FCSTD DOCUMENT  (FreeCAD 0.21R33668 +26 (Git))
Label: bushing sketch
License: All rights reserved
LicenseURL: https://en.wikipedia.org/wiki/All_rights_reserved
objects: Sketcher::SketchObject×3, PartDesign::Body×1
note: 4 computed .brp shape members not serialized (recipe doc carries the construction recipe); baked Part::Feature solids carry a one-line shape summary decoded from their .brp

FEATURE [Sketcher::SketchObject] Sketch
  FullyConstrained = false
  MapMode = 5
  Placement = pos=(0,0,0) rot=(1,0,0;1.5708rad)
  Support = -> [XZ_Plane]
  sketch-geometry (66):
    g0: LineSegment StartX=-3.3 StartY=0 StartZ=0 EndX=3.3 EndY=0 EndZ=0
    g1: LineSegment StartX=-3.3 StartY=0 StartZ=0 EndX=-3.3 EndY=-2 EndZ=0
    g2: LineSegment StartX=-3.3 StartY=-2 StartZ=0 EndX=-3.4 EndY=-2 EndZ=0
    g3: LineSegment StartX=-3.4 StartY=-2 StartZ=0 EndX=-3.4 EndY=-4.50007 EndZ=0
    g4: LineSegment StartX=-3.4 StartY=-4.50007 StartZ=0 EndX=-6.25 EndY=-4.50007 EndZ=0
    g5: LineSegment StartX=3.3 StartY=0 StartZ=0 EndX=3.3 EndY=-2 EndZ=0
    g6: LineSegment StartX=3.3 StartY=-2 StartZ=0 EndX=3.4 EndY=-2 EndZ=0
    g7: LineSegment StartX=3.4 StartY=-2 StartZ=0 EndX=3.4 EndY=-4.50007 EndZ=0
    g8: LineSegment StartX=3.4 StartY=-4.50007 StartZ=0 EndX=6.25 EndY=-4.50007 EndZ=0
    g9: LineSegment StartX=-3 StartY=0 StartZ=0 EndX=-3 EndY=1.5 EndZ=0
    g10: LineSegment StartX=-3 StartY=1.5 StartZ=0 EndX=-1.5 EndY=1.5 EndZ=0
    g11: LineSegment StartX=-1.5 StartY=1.5 StartZ=0 EndX=-1.5 EndY=8.5 EndZ=0
    g12: LineSegment StartX=-1.5 StartY=8.5 StartZ=0 EndX=3 EndY=8.5 EndZ=0
    g13: LineSegment StartX=3 StartY=8.5 StartZ=0 EndX=3 EndY=0 EndZ=0
    g14: LineSegment StartX=-3.15 StartY=0.999931 StartZ=0 EndX=-2.95 EndY=0.499931 EndZ=0
    g15: LineSegment StartX=-2.95 StartY=0.499931 StartZ=0 EndX=-3.15 EndY=-6.9e-05 EndZ=0
    g16: LineSegment StartX=-3.6 StartY=-6.9e-05 StartZ=0 EndX=-3.6 EndY=-1.00007 EndZ=0
    g17: LineSegment StartX=-3.6 StartY=-1.00007 StartZ=0 EndX=-3.3 EndY=-1.50007 EndZ=0
    g18: LineSegment StartX=-3.3 StartY=-1.50007 StartZ=0 EndX=-3.6 EndY=-2.00007 EndZ=0
    g19: LineSegment StartX=-3.6 StartY=-2.00007 StartZ=0 EndX=-3.6 EndY=-3.50007 EndZ=0
    g20: LineSegment StartX=-3.6 StartY=-3.50007 StartZ=0 EndX=-3.35 EndY=-4.00007 EndZ=0
    g21: LineSegment StartX=-3.35 StartY=-4.00007 StartZ=0 EndX=-3.85 EndY=-4.50007 EndZ=0
    g22: LineSegment StartX=-3.85 StartY=-4.50007 StartZ=0 EndX=-4.4 EndY=-4.50007 EndZ=0
    g23: LineSegment StartX=-4.4 StartY=-4.50007 StartZ=0 EndX=-4.4 EndY=-4.05007 EndZ=0
    g24: LineSegment StartX=-4.4 StartY=-4.05007 StartZ=0 EndX=-5.75 EndY=-4.05007 EndZ=0
    g25: LineSegment StartX=-5.75 StartY=-4.05007 StartZ=0 EndX=-5.75 EndY=-3.60007 EndZ=0
    g26: LineSegment StartX=-5.75 StartY=-3.60007 StartZ=0 EndX=-4.675 EndY=-3.60007 EndZ=0
    g27: LineSegment StartX=-4.675 StartY=-3.60007 StartZ=0 EndX=-4.675 EndY=-2.30007 EndZ=0
    g28: LineSegment StartX=-4.4 StartY=-2.02507 StartZ=0 EndX=-4.4 EndY=0.249931 EndZ=0
    g29: LineSegment StartX=-4.4 StartY=0.249931 StartZ=0 EndX=-3.65 EndY=0.999931 EndZ=0
    g30: LineSegment StartX=-3.65 StartY=0.999931 StartZ=0 EndX=-3.15 EndY=0.999931 EndZ=0
    g31: LineSegment StartX=-3.6 StartY=-6.9e-05 StartZ=0 EndX=-3.15 EndY=-6.9e-05 EndZ=0
    g32: LineSegment StartX=3.15 StartY=0.999931 StartZ=0 EndX=2.95 EndY=0.499931 EndZ=0
    g33: LineSegment StartX=2.95 StartY=0.499931 StartZ=0 EndX=3.15 EndY=-6.9e-05 EndZ=0
    g34: LineSegment StartX=3.5 StartY=-6.9e-05 StartZ=0 EndX=3.5 EndY=-1.00007 EndZ=0
    g35: LineSegment StartX=3.5 StartY=-1.00007 StartZ=0 EndX=3.3 EndY=-1.50007 EndZ=0
    g36: LineSegment StartX=3.3 StartY=-1.50007 StartZ=0 EndX=3.5 EndY=-2.00007 EndZ=0
    g37: LineSegment StartX=3.5 StartY=-2.00007 StartZ=0 EndX=3.5 EndY=-3.50007 EndZ=0
    g38: LineSegment StartX=3.5 StartY=-3.50007 StartZ=0 EndX=3.35 EndY=-4.00007 EndZ=0
    g39: LineSegment StartX=3.35 StartY=-4.00007 StartZ=0 EndX=3.85 EndY=-4.50007 EndZ=0
    g40: LineSegment StartX=3.85 StartY=-4.50007 StartZ=0 EndX=4.4 EndY=-4.50007 EndZ=0
    g41: LineSegment StartX=4.4 StartY=-4.50007 StartZ=0 EndX=4.4 EndY=-4.05007 EndZ=0
    g42: LineSegment StartX=4.4 StartY=-4.05007 StartZ=0 EndX=5.75 EndY=-4.05007 EndZ=0
    g43: LineSegment StartX=5.75 StartY=-4.05007 StartZ=0 EndX=5.75 EndY=-3.60007 EndZ=0
    g44: LineSegment StartX=5.75 StartY=-3.60007 StartZ=0 EndX=4.675 EndY=-3.60007 EndZ=0
    g45: LineSegment StartX=4.675 StartY=-3.60007 StartZ=0 EndX=4.675 EndY=-2.30007 EndZ=0
    g46: LineSegment StartX=4.4 StartY=-2.02507 StartZ=0 EndX=4.4 EndY=0.249931 EndZ=0
    g47: LineSegment StartX=4.4 StartY=0.249931 StartZ=0 EndX=3.65 EndY=0.999931 EndZ=0
    g48: LineSegment StartX=3.65 StartY=0.999931 StartZ=0 EndX=3.15 EndY=0.999931 EndZ=0
    g49: LineSegment StartX=3.5 StartY=-6.9e-05 StartZ=0 EndX=3.15 EndY=-6.9e-05 EndZ=0
    g50: LineSegment StartX=-6.25 StartY=-4.50007 StartZ=0 EndX=-6.25 EndY=-10.8 EndZ=0
    g51: LineSegment StartX=-6.25 StartY=-10.8 StartZ=0 EndX=6.25 EndY=-10.8 EndZ=0
    g52: LineSegment StartX=6.25 StartY=-10.8 StartZ=0 EndX=6.25 EndY=-4.50007 EndZ=0
    g53: LineSegment StartX=-13.8517 StartY=-10.8 StartZ=0 EndX=17.8649 EndY=-10.8 EndZ=0
    g54: LineSegment StartX=-12.656 StartY=-1.14 StartZ=0 EndX=12.2568 EndY=-1.14 EndZ=0
    g55: LineSegment StartX=12.2568 StartY=-1.14 StartZ=0 EndX=12.2568 EndY=-2.14 EndZ=0
    g56: LineSegment StartX=12.2568 StartY=-2.14 StartZ=0 EndX=-12.656 EndY=-2.14 EndZ=0
    g57: LineSegment StartX=-12.656 StartY=-2.14 StartZ=0 EndX=-12.656 EndY=-1.14 EndZ=0
    g58: LineSegment StartX=-4.675 StartY=-2.30007 StartZ=0 EndX=-4.4 EndY=-2.02507 EndZ=0
    g59: LineSegment StartX=4.675 StartY=-2.30007 StartZ=0 EndX=4.4 EndY=-2.02507 EndZ=0
    g60: LineSegment StartX=-13.8517 StartY=-10.8 StartZ=0 EndX=-13.8517 EndY=-12.24 EndZ=0
    g61: LineSegment StartX=-13.8517 StartY=-12.24 StartZ=0 EndX=17.8649 EndY=-12.24 EndZ=0
    g62: LineSegment StartX=17.8649 StartY=-12.24 StartZ=0 EndX=17.8649 EndY=-10.8 EndZ=0
    g63: LineSegment StartX=-2.44854 StartY=-12.24 StartZ=0 EndX=-2.44854 EndY=-16.14 EndZ=0
    g64: LineSegment StartX=-2.44854 StartY=-16.14 StartZ=0 EndX=4.63678 EndY=-16.14 EndZ=0
    g65: LineSegment StartX=4.63678 StartY=-16.14 StartZ=0 EndX=4.63678 EndY=-12.24 EndZ=0
  constraints (196):
    c: PointOnObject(g0,g-1)
    c: Symmetric(g0,g0,g-1)
    c: Coincident(g1,g0)
    c: Vertical(g1)
    c: Horizontal(g2)
    c: Coincident(g3,g2)
    c: Vertical(g3)
    c: Coincident(g4,g3)
    c: Horizontal(g4)
    c: Coincident(g2,g1)
    c: Coincident(g5,g0)
    c: Vertical(g5)
    c: Coincident(g6,g5)
    c: Horizontal(g6)
    c: Coincident(g7,g6)
    c: Vertical(g7)
    c: Coincident(g8,g7)
    c: Horizontal(g8)
    c: Equal(g6,g2)
    c: Equal(g3,g7)
    c: Equal(g8,g4)
    c: Equal(g5,g1)
    c: PointOnObject(g9,g0)
    c: Coincident(g10,g9)
    c: Vertical(g11)
    c: Horizontal(g12)
    c: Vertical(g13)
    c: Coincident(g13,g12)
    c: Coincident(g12,g11)
    c: Horizontal(g10)
    c: Vertical(g9)
    c: Coincident(g11,g10)
    c: DistanceY(g1,g1) = 2
    c: DistanceX(g0,g0) = 6.6
    c: DistanceX(g3,g7) = 6.8
    c: Symmetric(g9,g13,g-1)
    c: DistanceX(g9,g13) = 6
    c: DistanceX(g12,g12) = 4.5
    c: Coincident(g15,g14)
    c: Vertical(g16)
    c: Coincident(g18,g17)
    c: Coincident(g19,g18)
    c: Vertical(g19)
    c: Coincident(g20,g19)
    c: Coincident(g21,g20)
    c: Horizontal(g22)
    c: Coincident(g24,g23)
    c: Horizontal(g24)
    c: Coincident(g25,g24)
    c: Vertical(g25)
    c: Coincident(g26,g25)
    c: Horizontal(g26)
    c: Coincident(g27,g26)
    c: Vertical(g27)
    c: Vertical(g28)
    c: Coincident(g29,g28)
    c: Coincident(g30,g14)
    c: Coincident(g30,g29)
    c: Coincident(g21,g22)
    c: Horizontal(g30)
    c: DistanceX(g28,g29) = 0.75
    c: Angle(g29,g30) = 2.35619
    c: DistanceX(g30,g30) = 0.5
    c: DistanceX(g14,g-1) = 2.95
    c: DistanceY(g15,g14) = 1
    c: Equal(g14,g15)
    c: Coincident(g16,g17)
    c: Vertical(g16,g18)
    c: Equal(g17,g18)
    c: DistanceX(g17,g-1) = 3.3
    c: DistanceX(g20,g-1) = 3.35
    c: Coincident(g22,g23)
    c: Vertical(g23)
    c: Angle(g21,g22) = 2.35619
    c: DistanceY(g27,g27) = 1.3
    c: DistanceY(g23,g23) = 0.45
    c: DistanceX(g24,g-1) = 5.75
    c: DistanceX(g22,g-1) = 4.4
    c: DistanceY(g21,g19) = 1
    c: DistanceY(g18,g16) = 1
    c: DistanceX(g26,g-1) = 4.675
    c: DistanceY(g22,g15) = 4.5
    c: DistanceY(g21,g20) = 0.5
    c: DistanceY(g21,g17) = 3
    c: Coincident(g31,g16)
    c: Coincident(g31,g15)
    c: Horizontal(g31)
    c: DistanceX(g16,g-1) = 3.6
    c: Vertical(g14,g15)
    c: Coincident(g33,g32)
    c: Vertical(g34)
    c: Coincident(g36,g35)
    c: Coincident(g37,g36)
    c: Vertical(g37)
    c: Coincident(g38,g37)
    c: Coincident(g39,g38)
    c: Horizontal(g40)
    c: Coincident(g42,g41)
    c: Horizontal(g42)
    c: Coincident(g43,g42)
    c: Vertical(g43)
    c: Coincident(g44,g43)
    c: Horizontal(g44)
    c: Coincident(g45,g44)
    c: Vertical(g45)
    c: Vertical(g46)
    c: Coincident(g47,g46)
    c: Coincident(g48,g32)
    c: Coincident(g48,g47)
    c: Coincident(g39,g40)
    c: Horizontal(g48)
    c: Angle(g47,g48) = -2.35619
    c: Equal(g32,g33)
    c: Coincident(g34,g35)
    c: Equal(g35,g36)
    c: Coincident(g40,g41)
    c: Vertical(g41)
    c: Angle(g39,g40) = -2.35619
    c: Coincident(g49,g34)
    c: Coincident(g49,g33)
    c: Horizontal(g49)
    c: Equal(g16,g34)
    c: Equal(g19,g37)
    c: Equal(g22,g40)
    c: Equal(g14,g32)
    c: Equal(g30,g48)
    c: Equal(g29,g47)
    c: Equal(g45,g27)
    c: Equal(g26,g44)
    c: Equal(g25,g43)
    c: Equal(g24,g42)
    c: Equal(g23,g41)
    c: Vertical(g36,g34)
    c: Horizontal(g32,g14)
    c: Horizontal(g33,g15)
    c: Horizontal(g35,g17)
    c: Horizontal(g20,g38)
    c: DistanceX(g-1,g34) = 3.5
    c: DistanceX(g-1,g32) = 2.95
    c: DistanceX(g-1,g35) = 3.3
    c: DistanceX(g-1,g38) = 3.35
    c: DistanceY(g16,g16) = 1
    c: DistanceY(g22,g29) = 5.5
    c: DistanceX(g4,g8) = 12.5
    c: Coincident(g50,g4)
    c: Vertical(g50)
    c: Coincident(g51,g50)
    c: Horizontal(g51)
    c: Coincident(g52,g51)
    c: Coincident(g52,g8)
    c: Vertical(g52)
    c: Horizontal(g53)
    c: PointOnObject(g51,g53)
    c: Coincident(g54,g55)
    c: Coincident(g55,g56)
    c: Coincident(g56,g57)
    c: Coincident(g57,g54)
    c: Horizontal(g54)
    c: Horizontal(g56)
    c: Vertical(g55)
    c: Vertical(g57)
    c: DistanceY(g57,g57) = 1
    c: DistanceY(g4,g56) = 2.36007
    c: DistanceY(g26,g56) = 1.46007
    c: DistanceY(g22,g25) = 0.9
    c: Coincident(g58,g27)
    c: Coincident(g28,g58)
    c: Angle(g58) = 0.785398
    c: DistanceX(g28,g-1) = 4.4
    c: Coincident(g59,g45)
    c: Coincident(g46,g59)
    c: Angle(g59,g45) = 2.35619
    c: DistanceX(g-1,g46) = 4.4
    c: Horizontal(g39,g21)
    c: Coincident(g60,g53)
    c: Vertical(g60)
    c: Coincident(g61,g60)
    c: Horizontal(g61)
    c: Coincident(g62,g61)
    c: Coincident(g62,g53)
    c: Vertical(g62)
    c: PointOnObject(g63,g61)
    c: Vertical(g63)
    c: Coincident(g64,g63)
    c: Horizontal(g64)
    c: PointOnObject(g65,g61)
    c: Coincident(g65,g64)
    c: Vertical(g65)
    c: DistanceY(g60,g60) = 1.44
    c: DistanceY(g63,g63) = 3.9
    c: DistanceY(g65,g55) = 10.1
    c: DistanceY(g50,g0) = 10.8
    c: DistanceY(g25,g25) = 0.45
    c: DistanceY(g11,g11) = 7
    c: DistanceY(g9,g9) = 1.5
    c: PointOnObject(g21,g4)
FEATURE [Sketcher::SketchObject] Sketch001
  FullyConstrained = true
  MapMode = 5
  Support = -> [XY_Plane]
  sketch-geometry (9):
    g0: Circle CenterX=0 CenterY=0.075 CenterZ=0 NormalX=0 NormalY=0 NormalZ=1 AngleXU=0 Radius=4.875
    g1: Circle CenterX=0 CenterY=0.075 CenterZ=0 NormalX=0 NormalY=0 NormalZ=1 AngleXU=0 Radius=4.85
    g2: Circle CenterX=0 CenterY=0.075 CenterZ=0 NormalX=0 NormalY=0 NormalZ=1 AngleXU=0 Radius=4.825
    g3: Circle CenterX=0 CenterY=0 CenterZ=0 NormalX=0 NormalY=0 NormalZ=1 AngleXU=0 Radius=0.075
    g4: Circle CenterX=0 CenterY=0 CenterZ=0 NormalX=0 NormalY=0 NormalZ=1 AngleXU=0 Radius=4.95
    g5: Circle CenterX=0 CenterY=0 CenterZ=0 NormalX=0 NormalY=0 NormalZ=1 AngleXU=0 Radius=4.9
    g6: Circle CenterX=0 CenterY=0 CenterZ=0 NormalX=0 NormalY=0 NormalZ=1 AngleXU=0 Radius=4.675
    g7: LineSegment StartX=0 StartY=-4.675 StartZ=0 EndX=0 EndY=-4.75 EndZ=0
    g8: LineSegment StartX=0 StartY=4.675 StartZ=0 EndX=0 EndY=4.9 EndZ=0
  constraints (27):
    c: Coincident(g1,g0)
    c: Diameter(g0) = 9.75
    c: Diameter(g1) = 9.7
    c: Coincident(g2,g0)
    c: Diameter(g2) = 9.65
    c: Coincident(g3,g-1)
    c: Diameter(g3) = 0.15
    c: PointOnObject(g0,g3)
    c: Coincident(g4,g3)
    c: PointOnObject(g0,g-2)
    c: Tangent(g4,g0)
    c: Diameter(g4) = 9.9
    c: Coincident(g5,g3)
    c: Tangent(g5,g2)
    c: Diameter(g5) = 9.8
    c: Coincident(g6,g3)
    c: Diameter(g6) = 9.35
    c: PointOnObject(g7,g6)
    c: PointOnObject(g7,g2)
    c: Vertical(g7)
    c: PointOnObject(g7,g-2)
    c: DistanceY(g7,g7) = 0.075
    c: PointOnObject(g8,g6)
    c: PointOnObject(g8,g5)
    c: Vertical(g8)
    c: PointOnObject(g8,g-2)
    c: DistanceY(g8,g8) = 0.225
FEATURE [Sketcher::SketchObject] Sketch002
  FullyConstrained = false
  MapMode = 5
  Placement = pos=(0,0,0) rot=(1,0,0;1.5708rad)
  Support = -> [XZ_Plane]
  sketch-geometry (62):
    g0: LineSegment StartX=-3.35 StartY=0 StartZ=0 EndX=3.35 EndY=0 EndZ=0
    g1: LineSegment StartX=-3.35 StartY=0 StartZ=0 EndX=-3.35 EndY=-2 EndZ=0
    g2: LineSegment StartX=-3.35 StartY=-2 StartZ=0 EndX=-3.4 EndY=-2 EndZ=0
    g3: LineSegment StartX=-3.4 StartY=-2 StartZ=0 EndX=-3.4 EndY=-4.29691 EndZ=0
    g4: LineSegment StartX=-3.4 StartY=-4.29691 StartZ=0 EndX=-6.25 EndY=-4.29691 EndZ=0
    g5: LineSegment StartX=3.35 StartY=0 StartZ=0 EndX=3.35 EndY=-2 EndZ=0
    g6: LineSegment StartX=3.35 StartY=-2 StartZ=0 EndX=3.4 EndY=-2 EndZ=0
    g7: LineSegment StartX=3.4 StartY=-2 StartZ=0 EndX=3.4 EndY=-4.29691 EndZ=0
    g8: LineSegment StartX=3.4 StartY=-4.29691 StartZ=0 EndX=6.25 EndY=-4.29691 EndZ=0
    g9: LineSegment StartX=-3 StartY=0 StartZ=0 EndX=-3 EndY=1.5 EndZ=0
    g10: LineSegment StartX=-3 StartY=1.5 StartZ=0 EndX=-1.5 EndY=1.5 EndZ=0
    g11: LineSegment StartX=-1.5 StartY=1.5 StartZ=0 EndX=-1.5 EndY=8.5 EndZ=0
    g12: LineSegment StartX=-1.5 StartY=8.5 StartZ=0 EndX=3 EndY=8.5 EndZ=0
    g13: LineSegment StartX=3 StartY=8.5 StartZ=0 EndX=3 EndY=0 EndZ=0
    g14: LineSegment StartX=-3.15 StartY=1.20309 StartZ=0 EndX=-2.95 EndY=0.703087 EndZ=0
    g15: LineSegment StartX=-2.95 StartY=0.703087 StartZ=0 EndX=-3.15 EndY=0.203087 EndZ=0
    g16: LineSegment StartX=-3.3 StartY=-3.79691 StartZ=0 EndX=-3.8 EndY=-4.29691 EndZ=0
    g17: LineSegment StartX=-3.8 StartY=-4.29691 StartZ=0 EndX=-4.4 EndY=-4.29691 EndZ=0
    g18: LineSegment StartX=-4.4 StartY=-4.29691 StartZ=0 EndX=-4.4 EndY=-3.84691 EndZ=0
    g19: LineSegment StartX=-4.4 StartY=-3.84691 StartZ=0 EndX=-5.75 EndY=-3.84691 EndZ=0
    g20: LineSegment StartX=-5.75 StartY=-3.84691 StartZ=0 EndX=-5.75 EndY=-3.39691 EndZ=0
    g21: LineSegment StartX=-5.75 StartY=-3.39691 StartZ=0 EndX=-4.675 EndY=-3.39691 EndZ=0
    g22: LineSegment StartX=-4.675 StartY=-3.39691 StartZ=0 EndX=-4.675 EndY=-2.09691 EndZ=0
    g23: LineSegment StartX=-4.4 StartY=-1.82191 StartZ=0 EndX=-4.4 EndY=0.453087 EndZ=0
    g24: LineSegment StartX=-4.4 StartY=0.453087 StartZ=0 EndX=-3.65 EndY=1.20309 EndZ=0
    g25: LineSegment StartX=-3.65 StartY=1.20309 StartZ=0 EndX=-3.15 EndY=1.20309 EndZ=0
    g26: LineSegment StartX=-3.3 StartY=0.203087 StartZ=0 EndX=-3.15 EndY=0.203087 EndZ=0
    g27: LineSegment StartX=3.15 StartY=1.20309 StartZ=0 EndX=2.95 EndY=0.703087 EndZ=0
    g28: LineSegment StartX=2.95 StartY=0.703087 StartZ=0 EndX=3.15 EndY=0.203087 EndZ=0
    g29: LineSegment StartX=3.5 StartY=0.203087 StartZ=0 EndX=3.5 EndY=-1.00007 EndZ=0
    g30: LineSegment StartX=3.5 StartY=-1.00007 StartZ=0 EndX=3.3 EndY=-1.50007 EndZ=0
    g31: LineSegment StartX=3.3 StartY=-1.50007 StartZ=0 EndX=3.5 EndY=-2.00007 EndZ=0
    g32: LineSegment StartX=3.5 StartY=-2.00007 StartZ=0 EndX=3.5 EndY=-3.50007 EndZ=0
    g33: LineSegment StartX=3.5 StartY=-3.50007 StartZ=0 EndX=3.35 EndY=-3.79691 EndZ=0
    g34: LineSegment StartX=3.35 StartY=-3.79691 StartZ=0 EndX=3.85 EndY=-4.29691 EndZ=0
    g35: LineSegment StartX=3.85 StartY=-4.29691 StartZ=0 EndX=4.45 EndY=-4.29691 EndZ=0
    g36: LineSegment StartX=4.45 StartY=-4.29691 StartZ=0 EndX=4.45 EndY=-3.84691 EndZ=0
    g37: LineSegment StartX=4.45 StartY=-3.84691 StartZ=0 EndX=5.8 EndY=-3.84691 EndZ=0
    g38: LineSegment StartX=5.8 StartY=-3.84691 StartZ=0 EndX=5.8 EndY=-3.39691 EndZ=0
    g39: LineSegment StartX=5.8 StartY=-3.39691 StartZ=0 EndX=4.725 EndY=-3.39691 EndZ=0
    g40: LineSegment StartX=4.725 StartY=-3.39691 StartZ=0 EndX=4.725 EndY=-2.09691 EndZ=0
    g41: LineSegment StartX=4.4 StartY=-1.77191 StartZ=0 EndX=4.4 EndY=0.453087 EndZ=0
    g42: LineSegment StartX=4.4 StartY=0.453087 StartZ=0 EndX=3.65 EndY=1.20309 EndZ=0
    g43: LineSegment StartX=3.65 StartY=1.20309 StartZ=0 EndX=3.15 EndY=1.20309 EndZ=0
    g44: LineSegment StartX=3.5 StartY=0.203087 StartZ=0 EndX=3.15 EndY=0.203087 EndZ=0
    g45: LineSegment StartX=-6.25 StartY=-4.29691 StartZ=0 EndX=-6.25 EndY=-10.8 EndZ=0
    g46: LineSegment StartX=-6.25 StartY=-10.8 StartZ=0 EndX=6.25 EndY=-10.8 EndZ=0
    g47: LineSegment StartX=6.25 StartY=-10.8 StartZ=0 EndX=6.25 EndY=-4.29691 EndZ=0
    g48: LineSegment StartX=-13.8517 StartY=-10.8 StartZ=0 EndX=17.8649 EndY=-10.8 EndZ=0
    g49: LineSegment StartX=-12.656 StartY=-1.14 StartZ=0 EndX=12.2568 EndY=-1.14 EndZ=0
    g50: LineSegment StartX=12.2568 StartY=-1.14 StartZ=0 EndX=12.2568 EndY=-2.14 EndZ=0
    g51: LineSegment StartX=12.2568 StartY=-2.14 StartZ=0 EndX=-12.656 EndY=-2.14 EndZ=0
    g52: LineSegment StartX=-12.656 StartY=-2.14 StartZ=0 EndX=-12.656 EndY=-1.14 EndZ=0
    g53: LineSegment StartX=-4.675 StartY=-2.09691 StartZ=0 EndX=-4.4 EndY=-1.82191 EndZ=0
    g54: LineSegment StartX=4.725 StartY=-2.09691 StartZ=0 EndX=4.4 EndY=-1.77191 EndZ=0
    g55: LineSegment StartX=-13.8517 StartY=-10.8 StartZ=0 EndX=-13.8517 EndY=-12.24 EndZ=0
    g56: LineSegment StartX=-13.8517 StartY=-12.24 StartZ=0 EndX=17.8649 EndY=-12.24 EndZ=0
    g57: LineSegment StartX=17.8649 StartY=-12.24 StartZ=0 EndX=17.8649 EndY=-10.8 EndZ=0
    g58: LineSegment StartX=-2.44854 StartY=-12.24 StartZ=0 EndX=-2.44854 EndY=-16.14 EndZ=0
    g59: LineSegment StartX=-2.44854 StartY=-16.14 StartZ=0 EndX=4.63678 EndY=-16.14 EndZ=0
    g60: LineSegment StartX=4.63678 StartY=-16.14 StartZ=0 EndX=4.63678 EndY=-12.24 EndZ=0
    g61: LineSegment StartX=-3.3 StartY=-3.79691 StartZ=0 EndX=-3.3 EndY=0.203087 EndZ=0
  constraints (180):
    c: PointOnObject(g0,g-1)
    c: Symmetric(g0,g0,g-1)
    c: Coincident(g1,g0)
    c: Vertical(g1)
    c: Horizontal(g2)
    c: Coincident(g3,g2)
    c: Vertical(g3)
    c: Coincident(g4,g3)
    c: Horizontal(g4)
    c: Coincident(g2,g1)
    c: Coincident(g5,g0)
    c: Vertical(g5)
    c: Coincident(g6,g5)
    c: Horizontal(g6)
    c: Coincident(g7,g6)
    c: Vertical(g7)
    c: Coincident(g8,g7)
    c: Horizontal(g8)
    c: Equal(g6,g2)
    c: Equal(g3,g7)
    c: Equal(g8,g4)
    c: Equal(g5,g1)
    c: PointOnObject(g9,g0)
    c: Coincident(g10,g9)
    c: Vertical(g11)
    c: Horizontal(g12)
    c: Vertical(g13)
    c: Coincident(g13,g12)
    c: Coincident(g12,g11)
    c: Horizontal(g10)
    c: Vertical(g9)
    c: Coincident(g11,g10)
    c: DistanceY(g1,g1) = 2
    c: DistanceX(g0,g0) = 6.7
    c: DistanceX(g3,g7) = 6.8
    c: Symmetric(g9,g13,g-1)
    c: DistanceX(g9,g13) = 6
    c: DistanceX(g12,g12) = 4.5
    c: Coincident(g15,g14)
    c: Horizontal(g17)
    c: Coincident(g19,g18)
    c: Horizontal(g19)
    c: Coincident(g20,g19)
    c: Vertical(g20)
    c: Coincident(g21,g20)
    c: Horizontal(g21)
    c: Coincident(g22,g21)
    c: Vertical(g22)
    c: Vertical(g23)
    c: Coincident(g24,g23)
    c: Coincident(g25,g14)
    c: Coincident(g25,g24)
    c: Coincident(g16,g17)
    c: Horizontal(g25)
    c: DistanceX(g23,g24) = 0.75
    c: Angle(g24,g25) = 2.35619
    c: DistanceX(g25,g25) = 0.5
    c: DistanceX(g14,g-1) = 2.95
    c: DistanceY(g15,g14) = 1
    c: Equal(g14,g15)
    c: DistanceX(g16,g-1) = 3.3
    c: Coincident(g17,g18)
    c: Vertical(g18)
    c: Angle(g16,g17) = 2.35619
    c: DistanceY(g22,g22) = 1.3
    c: DistanceY(g18,g18) = 0.45
    c: DistanceX(g19,g-1) = 5.75
    c: DistanceX(g17,g-1) = 4.4
    c: DistanceX(g21,g-1) = 4.675
    c: DistanceY(g17,g15) = 4.5
    c: DistanceY(g16,g16) = 0.5
    c: Coincident(g26,g15)
    c: Horizontal(g26)
    c: Vertical(g14,g15)
    c: Coincident(g28,g27)
    c: Vertical(g29)
    c: Coincident(g31,g30)
    c: Coincident(g32,g31)
    c: Vertical(g32)
    c: Coincident(g33,g32)
    c: Coincident(g34,g33)
    c: Horizontal(g35)
    c: Coincident(g37,g36)
    c: Horizontal(g37)
    c: Coincident(g38,g37)
    c: Vertical(g38)
    c: Coincident(g39,g38)
    c: Horizontal(g39)
    c: Coincident(g40,g39)
    c: Vertical(g40)
    c: Vertical(g41)
    c: Coincident(g42,g41)
    c: Coincident(g43,g27)
    c: Coincident(g43,g42)
    c: Coincident(g34,g35)
    c: Horizontal(g43)
    c: Angle(g42,g43) = -2.35619
    c: Equal(g27,g28)
    c: Coincident(g29,g30)
    c: Equal(g30,g31)
    c: Coincident(g35,g36)
    c: Vertical(g36)
    c: Angle(g34,g35) = -2.35619
    c: Coincident(g44,g29)
    c: Coincident(g44,g28)
    c: Horizontal(g44)
    c: Equal(g17,g35)
    c: Equal(g14,g27)
    c: Equal(g25,g43)
    c: Equal(g24,g42)
    c: Equal(g40,g22)
    c: Equal(g21,g39)
    c: Equal(g20,g38)
    c: Equal(g19,g37)
    c: Equal(g18,g36)
    c: Vertical(g31,g29)
    c: Horizontal(g27,g14)
    c: Horizontal(g28,g15)
    c: Horizontal(g16,g33)
    c: DistanceX(g-1,g29) = 3.5
    c: DistanceX(g-1,g27) = 2.95
    c: DistanceX(g-1,g30) = 3.3
    c: DistanceX(g-1,g33) = 3.35
    c: DistanceY(g17,g24) = 5.5
    c: DistanceX(g4,g8) = 12.5
    c: Coincident(g45,g4)
    c: Vertical(g45)
    c: Coincident(g46,g45)
    c: Horizontal(g46)
    c: Coincident(g47,g46)
    c: Coincident(g47,g8)
    c: Vertical(g47)
    c: Horizontal(g48)
    c: PointOnObject(g46,g48)
    c: Coincident(g49,g50)
    c: Coincident(g50,g51)
    c: Coincident(g51,g52)
    c: Coincident(g52,g49)
    c: Horizontal(g49)
    c: Horizontal(g51)
    c: Vertical(g50)
    c: Vertical(g52)
    c: DistanceY(g52,g52) = 1
    c: DistanceY(g4,g51) = 2.15691
    c: DistanceY(g21,g51) = 1.25691
    c: DistanceY(g17,g20) = 0.9
    c: Coincident(g53,g22)
    c: Coincident(g23,g53)
    c: Angle(g53) = 0.785398
    c: DistanceX(g23,g-1) = 4.4
    c: Coincident(g54,g40)
    c: Coincident(g41,g54)
    c: Angle(g54,g40) = 2.35619
    c: DistanceX(g-1,g41) = 4.4
    c: Horizontal(g34,g16)
    c: Coincident(g55,g48)
    c: Vertical(g55)
    c: Coincident(g56,g55)
    c: Horizontal(g56)
    c: Coincident(g57,g56)
    c: Coincident(g57,g48)
    c: Vertical(g57)
    c: PointOnObject(g58,g56)
    c: Vertical(g58)
    c: Coincident(g59,g58)
    c: Horizontal(g59)
    c: PointOnObject(g60,g56)
    c: Coincident(g60,g59)
    c: Vertical(g60)
    c: DistanceY(g55,g55) = 1.44
    c: DistanceY(g58,g58) = 3.9
    c: DistanceY(g60,g50) = 10.1
    c: DistanceY(g45,g0) = 10.8
    c: DistanceY(g20,g20) = 0.45
    c: DistanceY(g11,g11) = 7
    c: DistanceY(g9,g9) = 1.5
    c: PointOnObject(g16,g4)
    c: Vertical(g61)
    c: Coincident(g61,g26)
    c: Coincident(g16,g61)
FEATURE [PartDesign::Body] Body
  Group = -> [Sketch,Sketch001,Sketch002]
  Origin = -> Origin
